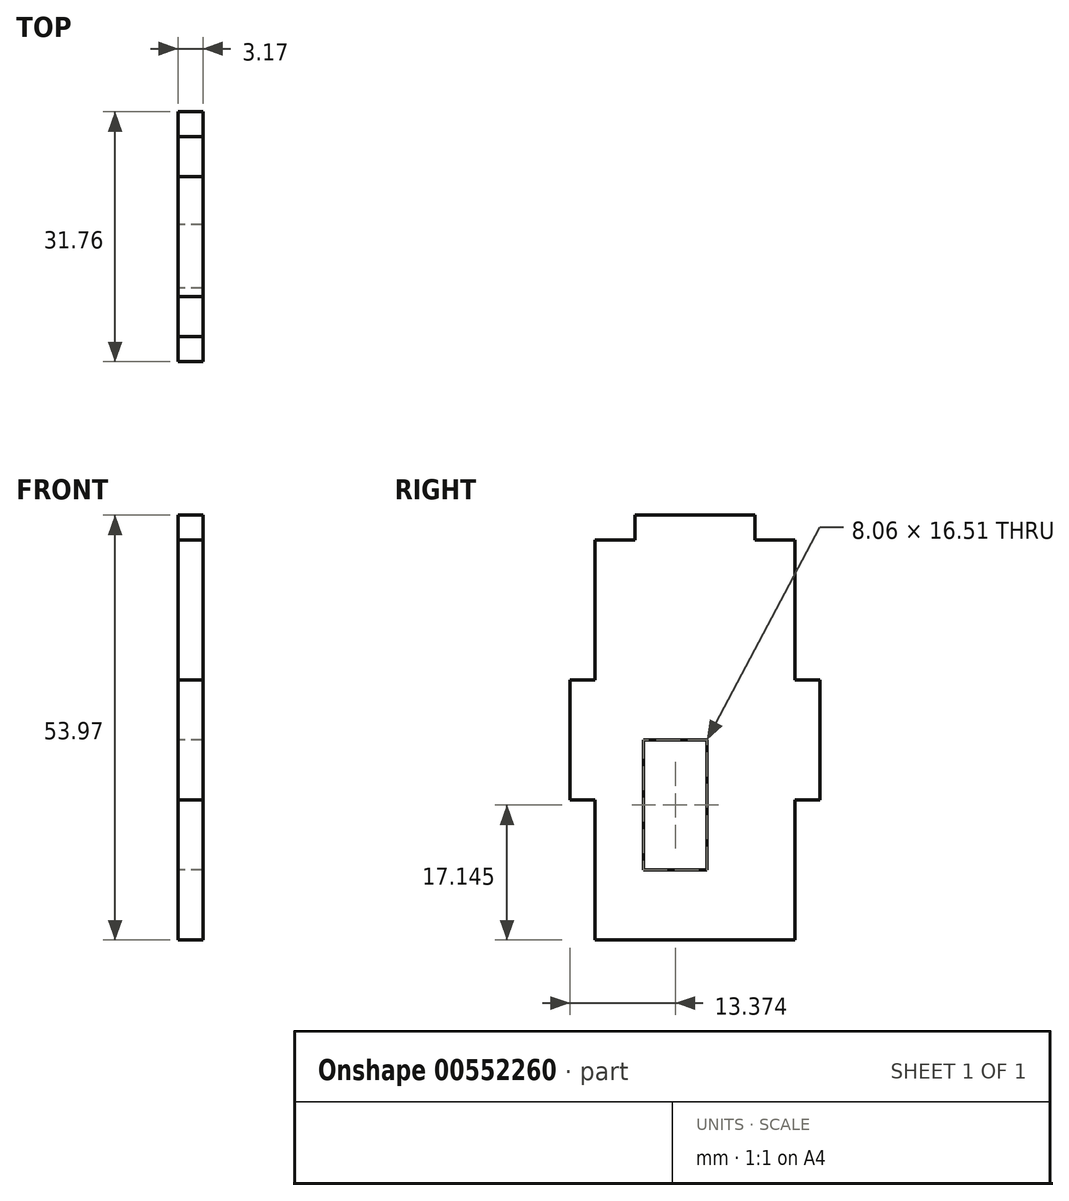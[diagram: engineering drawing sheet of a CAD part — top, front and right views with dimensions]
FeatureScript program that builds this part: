
annotation { "Feature Type Name" : "Feature", "Feature Type Description" : "" }
export const myFeature = defineFeature(function(context is Context, id is Id, definition is map)
    precondition{}
    {
        {
            var Q0;
            Q0=qCreatedBy(makeId("Right.planeOp"),FACE);
            var sketch = newSketch(context, id + "F0", { "sketchPlane" : qUnion([Q0])});
            skLineSegment(sketch, "E0.bottom", {"start": v(-12.7, -25.4) * mm, "end": v(12.7, -25.4) * mm});
            skPoint(sketch, "E0.middle", {"position": v(0, 0) * mm});
            skLineSegment(sketch, "E1", {"start": v(-7.62, 25.4) * mm, "end": v(-12.7, 25.4) * mm});
            skLineSegment(sketch, "E2", {"start": v(7.62, 25.4) * mm, "end": v(12.7, 25.4) * mm});
            skLineSegment(sketch, "E3", {"start": v(12.7, 25.4) * mm, "end": v(12.7, 7.62) * mm});
            skLineSegment(sketch, "E4", {"start": v(12.7, -7.62) * mm, "end": v(12.7, -25.4) * mm});
            skLineSegment(sketch, "E5", {"start": v(-12.7, 25.4) * mm, "end": v(-12.7, 7.62) * mm});
            skLineSegment(sketch, "E6", {"start": v(-12.7, -7.62) * mm, "end": v(-12.7, -25.4) * mm});
            skLineSegment(sketch, "E7", {"start": v(1.52, 0) * mm, "end": v(1.52, -16.51) * mm});
            skLineSegment(sketch, "E8", {"start": v(-7.62, 28.58) * mm, "end": v(7.62, 28.58) * mm});
            skLineSegment(sketch, "E9", {"start": v(7.62, 28.58) * mm, "end": v(7.62, 25.4) * mm});
            skLineSegment(sketch, "E10", {"start": v(15.88, 7.62) * mm, "end": v(15.88, -7.62) * mm});
            skLineSegment(sketch, "E11", {"start": v(15.88, -7.62) * mm, "end": v(12.7, -7.62) * mm});
            skLineSegment(sketch, "E12", {"start": v(15.88, 7.62) * mm, "end": v(12.7, 7.62) * mm});
            skLineSegment(sketch, "E13", {"start": v(-7.62, 28.58) * mm, "end": v(-7.62, 25.4) * mm});
            skLineSegment(sketch, "E14", {"start": v(-15.88, -7.62) * mm, "end": v(-15.88, 7.62) * mm});
            skLineSegment(sketch, "E15", {"start": v(-15.88, 7.62) * mm, "end": v(-12.7, 7.62) * mm});
            skLineSegment(sketch, "E16", {"start": v(-12.7, -7.62) * mm, "end": v(-15.88, -7.62) * mm});
            skLineSegment(sketch, "E17", {"start": v(-6.54, -16.51) * mm, "end": v(-6.54, 0) * mm});
            skLineSegment(sketch, "E18", {"start": v(0, 0) * mm, "end": v(-6.54, 0) * mm});
            skLineSegment(sketch, "E19", {"start": v(0.32, -16.51) * mm, "end": v(-6.54, -16.51) * mm});
            skLineSegment(sketch, "E20", {"start": v(0.32, -16.51) * mm, "end": v(1.52, -16.51) * mm});
            skLineSegment(sketch, "E21", {"start": v(0, 0) * mm, "end": v(1.52, 0) * mm});
            skSolve(sketch);
        }
        {
            var Q0;
            Q0=makeQuery(id+"F0.imprint","IMPRINT",FACE,{"disambiguationData":[TD([[makeQuery(id+"F0.imprint","IMPRINT",EDGE,{"derivedFrom":sQuery(id+"F0.wireOp",EDGE,"E0.bottom")}),1.0]])]});
            extrude(context, id + "F1", {"entities" : qUnion([Q0]), "depth" : 3.17 * mm, "offsetDistance" : 25.4 * mm});
        }
    });
